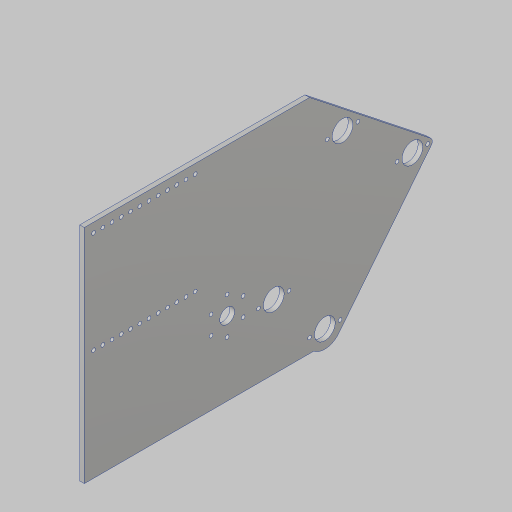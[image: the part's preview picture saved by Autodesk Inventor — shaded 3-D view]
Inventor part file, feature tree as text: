
AUTODESK INVENTOR PART (.ipt)
format: ipt  version: 2023.5 (Build 275446000, 446)  size: 255,488 bytes
history: native  units: in
note: dims shown in document units (in); Inventor stores cm internally (conversion verified against a paired STEP export)
features: sketch x4, extrude x2, hole x2, projected_geometry x2
ambient origin geometry x8: Origin, YZ Plane, XZ Plane, XY Plane, X Axis, Y Axis, Z Axis, Center Point
bodies: Solid1 (feature_tree)
feature tree (10):
  sketch  "Sketch2"  dims[d2=5.0in d3=3.0in]
  extrude  "Extrusion1"  Depth=3.0in
  sketch  "Sketch3"  dims[d4=0.5in d5=12.0in]
  sketch  "Sketch4"  dims[d6=4.5in d7=1.25in]
  extrude  "Extrusion2"  Depth=12.0in
  hole  "Hole1"  [1 undecoded]
  hole  "Hole3"  [1 undecoded]
  sketch  "Sketch6"  dims[d8=2.0in d9=5.0in d10=6.875in d11=1.115in d12=1.25in d13=1.0in d14=3.8976in d16=8.7496in d17=5.0in d18=4.7835in d27=7.0in d33=0.25in d34=0.0in d36=3.0in d37=5.0in d38=0.25in d40=2.0in d41=0.75in d42=16.0in d43=5.0in d44=0.313in d45=0.313in d46=1.5748in d48=1.0in d49=0.3937in d51=1.0in d53=0.8in d55=4.0in d56=1.0in d57=0.0in d58=2.0in d59=2.3622in d61=360.0deg d63=0.201in d64=0.75in d65=0.385in d66=0.25in d67=0.5635in d68=1.0in d69=0.8108in d70=7.1093in d80=1.655in d81=1.655in d82=1.655in d83=1.655in d84=0.5in d85=0.25in d86=0.25in d87=0.4in d89=0.201in d90=0.75in d91=0.385in d92=0.25in d93=0.5635in d94=1.0in d95=0.8108in d97=6.0in d98=0.5in d101=0.5in d102=4.7244in d104=0.5in d105=0.3937in d107=1.0in d109=4.5in d110=11.875in d111=0.75in d112=3.75in d113=12.0in d114=5.5in d115=5.0in d116=6.0in d117=2.5709in]
  projected_geometry  "Project Cut Edges1"
  projected_geometry  "Project Cut Edges2"
note: 2 required parameter values undecoded (feature->parameter linkage not recoverable at this tier; creation-order binding heuristic only, values carry confidence <= 0.55)
